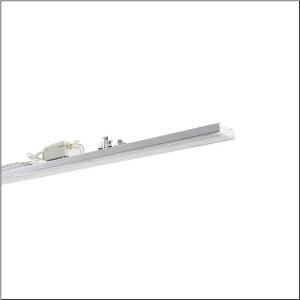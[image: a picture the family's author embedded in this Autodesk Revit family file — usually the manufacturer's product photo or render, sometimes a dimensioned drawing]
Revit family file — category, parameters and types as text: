
# Revit family: licross_21_recessed_mo_52tl18vn455g
name_source: partatom
category: Lighting Fixtures
units: mm (PartAtom-declared; Revit-internal decimal feet)

## family parameters
Cut with Voids When Loaded = No
Host = Face
Light Source = No
Part Type = Normal
Room Calculation Point = No
Round Connector Dimension = Use Diameter
Shared = No

## types (1)
- --- (1 x LED, 5500 lm, 30.5 W, 4000K)
    Apparent Load = 31 VA
    CIE Flux Codes = 79 95 99 100 100
    Color Rendering = 80
    Color Temperature = 4000K
    Default Elevation = 1800 mm
    Description = Licross 21 Recessed MO, luminaire insert, of sheet steel, galvanised, coil coated, white, length: 1.500mm, width: 66mm, height: 67mm, LED rated luminous flux: 5.500lm, light colour: 840, SDCM (Standard Deviation of Colour Matching)MacAdam ≤ 3 SDCM (initial), control gear: DALI 2, CLO, with plug, 5-pole, with phase selection, mains connection: 220..240V, AC, 50/60Hz, start of lifetime: 31W, end of service life: 36W, internal wiring halogen-free, primary optical cover: cover, of PMMA, light emission: direct distribution, primary light characteristic: symmetric, protection rating (complete): IP40, insulation class (complete): insulation class I (protective earthing), certification: CE, ENEC, VDE, UKCA, protection symbol: D if used in an environment without relevant dust loads with corresponding accessories, impact resistance: IK06, permissible ambient temperature for indoor applications: -25..+45°C, corresponds to IFS (International Featured Standards) requirements for safety and quality in the food industry, reducing of maximum allowable ambient temperature of 5°C with ceiling mounting, LABS conformity tested according to VDMA 24364:2018-05, The light source and the operating device comply with the requirements of the Ecodesign Regulation (EU) 2019/2020 and are replaceable in accordance with this regulation, packaging unit: 1 piece
    Height = 58 mm
    Lamp = 1 x LED
    Lamp Light Flux = 5500 lm
    Lamp Power = 30.5 W
    Lamp count = 1
    Length = 1500 mm
    Luminous efficacy = 180 lm/W
    Manufacturer = Siteco
    ModVariant = No
    Model = 52TL18VN455G
    Mounting Place = Ceiling
    Mounting Type = Pendant
    Number of Poles = 1
    OnlyDefault = Yes
    Power Factor = 1
    Product Name = Licross 21 Recessed MO
    Product group = luminaire insert | ceiling pendant
    ProductGroupID = 901
    Protection Class = Protection class I
    Protection Degree = IP 40
    RLX_Detail_Level = 1
    RLX_Emergency_Light_Flux = 0 lm
    RLX_Emergency_Type = 0
    RLX_Emergency_Type_DB = No
    RlxData = <blob elided: 24221 chars, md5=c0a967fc>
    Socket = socket
    Standby Power = 0 W
    System Light Flux = 5500 lm
    System Power = 31 W
    Type Comments = factory setting: luminous flux: 100 % | dim-lin: 254 | 206 mA
    Type Image = l_1296930.jpg
    URL = http://relux.com
    VarID = @adj_088801
    Voltage = 0 V
    Weight = 0.00 kg
    Width = 66 mm

## geometry (parser evidence)
native form markers: Blend x4, Sweep x13
no freeform markers — native parametric forms only
